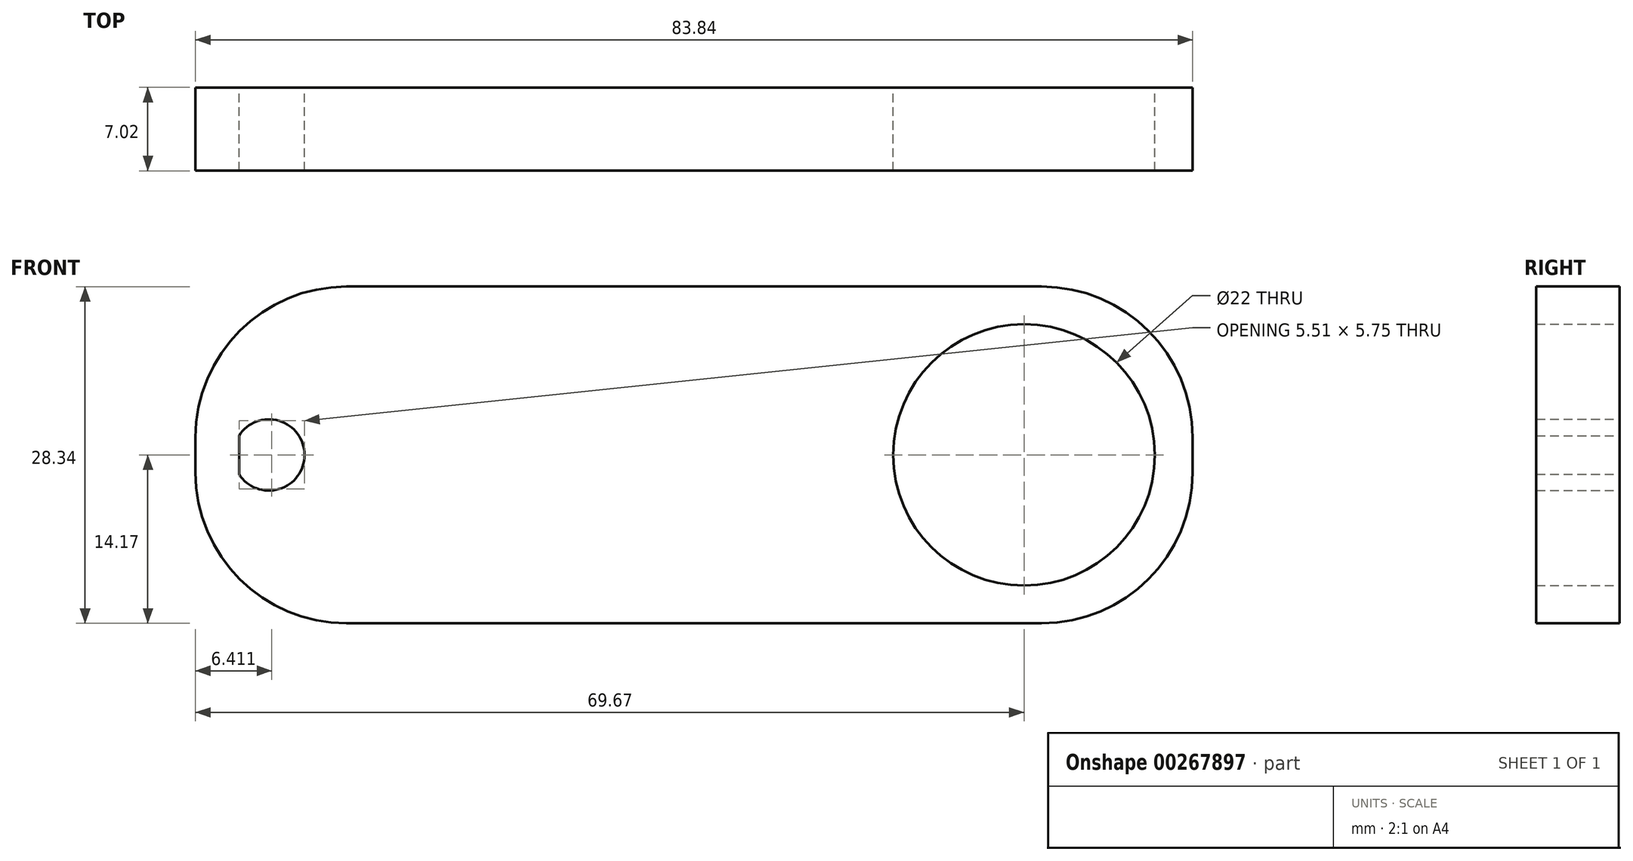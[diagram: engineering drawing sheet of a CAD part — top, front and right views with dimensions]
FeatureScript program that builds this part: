
annotation { "Feature Type Name" : "Feature", "Feature Type Description" : "" }
export const myFeature = defineFeature(function(context is Context, id is Id, definition is map)
    precondition{}
    {
        {
            var Q0;
            Q0=qCreatedBy(makeId("Front.planeOp"),FACE);
            var sketch = newSketch(context, id + "F0", { "sketchPlane" : qUnion([Q0])});
            skLineSegment(sketch, "E0.bottom", {"start": v(45.92, 14.17) * mm, "end": v(-45.92, 14.17) * mm});
            skLineSegment(sketch, "E0.top", {"start": v(45.92, -14.17) * mm, "end": v(-45.92, -14.17) * mm});
            skLineSegment(sketch, "E0.left", {"start": v(45.92, 14.17) * mm, "end": v(45.92, -14.17) * mm});
            skLineSegment(sketch, "E0.right", {"start": v(-45.92, 14.17) * mm, "end": v(-45.92, -14.17) * mm});
            skPoint(sketch, "E0.middle", {"position": v(0, 0) * mm});
            skCircle(sketch, "E1", {"center": v(-31.75, 0) * mm, "radius": 3 * mm});
            skCircle(sketch, "E2.MirrorC", {"center": v(31.75, 0) * mm, "radius": 11 * mm});
            skLineSegment(sketch, "E3", {"start": v(-34.26, 1.63) * mm, "end": v(-34.26, -1.63) * mm});
            skLineSegment(sketch, "E4", {"start": v(-37.92, 14.17) * mm, "end": v(-37.92, -14.17) * mm});
            skSolve(sketch);
        }
        {
            var Q0;
            {var subQ4=sQuery(id+"F0.wireOp",EDGE,"E0.left");Q0=makeQuery(id+"F0.imprint","IMPRINT",FACE,{"disambiguationData":[TD([[makeQuery(id+"F0.imprint","IMPRINT",EDGE,{"derivedFrom":subQ4}),-1.0]])]});}
            var Q1;
            {var subQ0=sQuery(id+"F0.wireOp",EDGE,"E3");Q1=makeQuery(id+"F0.imprint","IMPRINT",FACE,{"disambiguationData":[TD([[makeQuery(id+"F0.imprint","IMPRINT",EDGE,{"derivedFrom":subQ0}),-1.0]])]});}
            extrude(context, id + "F1", {"entities" : qUnion([Q0, Q1]), "endBound" : BoundingType.SYMMETRIC, "depth" : 7 * mm});
        }
        {
            var Q0;
            Q0=makeQuery(id+"F1.opExtrude","SWEPT_EDGE",EDGE,{"disambiguationData":[OSD([sQuery(id+"F0.wireOp",EDGE,"E0.bottom"),sQuery(id+"F0.wireOp",EDGE,"E4")])]});
            var Q1;
            Q1=makeQuery(id+"F1.opExtrude","SWEPT_EDGE",EDGE,{"disambiguationData":[OSD([sQuery(id+"F0.wireOp",EDGE,"E0.top"),sQuery(id+"F0.wireOp",EDGE,"E4")])]});
            var Q2;
            Q2=makeQuery(id+"F1.opExtrude","SWEPT_EDGE",EDGE,{"disambiguationData":[OSD([sQuery(id+"F0.wireOp",EDGE,"E0.bottom"),sQuery(id+"F0.wireOp",EDGE,"E0.left")])]});
            var Q3;
            Q3=makeQuery(id+"F1.opExtrude","SWEPT_EDGE",EDGE,{"disambiguationData":[OSD([sQuery(id+"F0.wireOp",EDGE,"E0.top"),sQuery(id+"F0.wireOp",EDGE,"E0.left")])]});
            fillet(context, id + "F2", {"entities" : qUnion([Q0, Q1, Q2, Q3]), "radius" : 12.7 * mm, "tangentPropagation" : true, "allowEdgeOverflow" : false});
        }
    });
